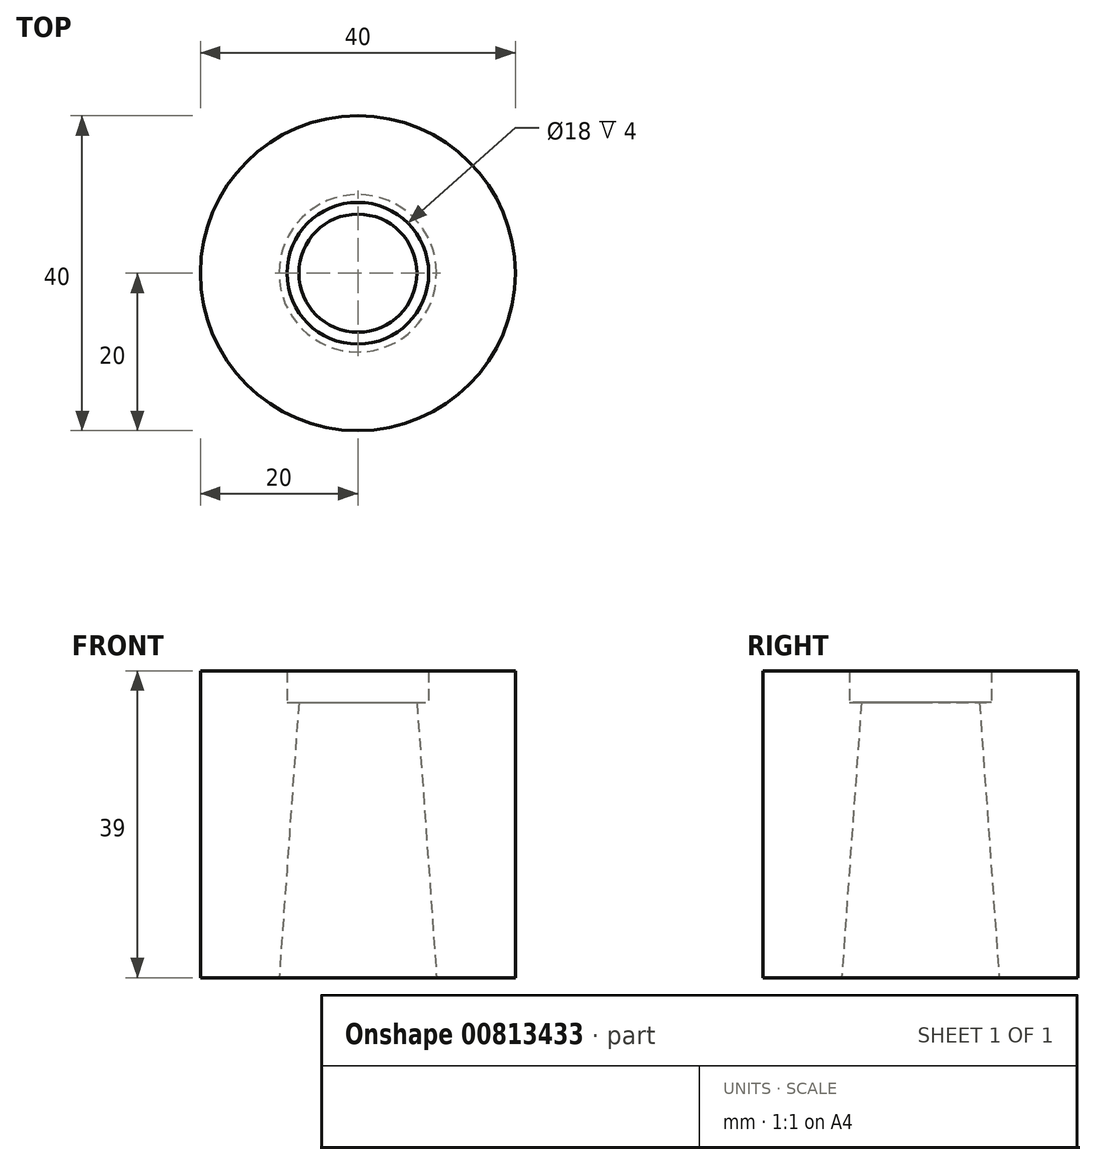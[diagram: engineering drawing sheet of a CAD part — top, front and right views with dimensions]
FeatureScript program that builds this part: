
annotation { "Feature Type Name" : "Feature", "Feature Type Description" : "" }
export const myFeature = defineFeature(function(context is Context, id is Id, definition is map)
    precondition{}
    {
        {
            var Q0;
            Q0=qCreatedBy(makeId("Front.planeOp"),FACE);
            var sketch = newSketch(context, id + "F0", { "sketchPlane" : qUnion([Q0])});
            skLineSegment(sketch, "E0", {"start": v(-7.5, 35) * mm, "end": v(-9, 35) * mm});
            skLineSegment(sketch, "E1", {"start": v(-9, 35) * mm, "end": v(-9, 39) * mm});
            skLineSegment(sketch, "E2", {"start": v(-9, 39) * mm, "end": v(-20, 39) * mm});
            skLineSegment(sketch, "E3", {"start": v(-20, 39) * mm, "end": v(-20, 0) * mm});
            skLineSegment(sketch, "E4", {"start": v(-20, 0) * mm, "end": v(-10, 0) * mm});
            skLineSegment(sketch, "E5", {"start": v(0, 0) * mm, "end": v(0, 40.66) * mm, "construction": true});
            skLineSegment(sketch, "E6", {"start": v(-7.5, 35) * mm, "end": v(-10, 0) * mm});
            skSolve(sketch);
        }
        {
            var Q0;
            Q0=makeQuery(id+"F0.imprint","IMPRINT",FACE,{"disambiguationData":[TD([[makeQuery(id+"F0.imprint","IMPRINT",EDGE,{"derivedFrom":sQuery(id+"F0.wireOp",EDGE,"E0")}),1.0]])]});
            var Q1;
            Q1=sQuery(id+"F0.wireOp",EDGE,"E5");
            revolve(context, id + "F1", {"surfaceOperationType" : NewSurfaceOperationType.NEW, "entities" : qUnion([Q0]), "axis" : qUnion([Q1]), "revolveType" : RevolveType.FULL});
        }
    });
